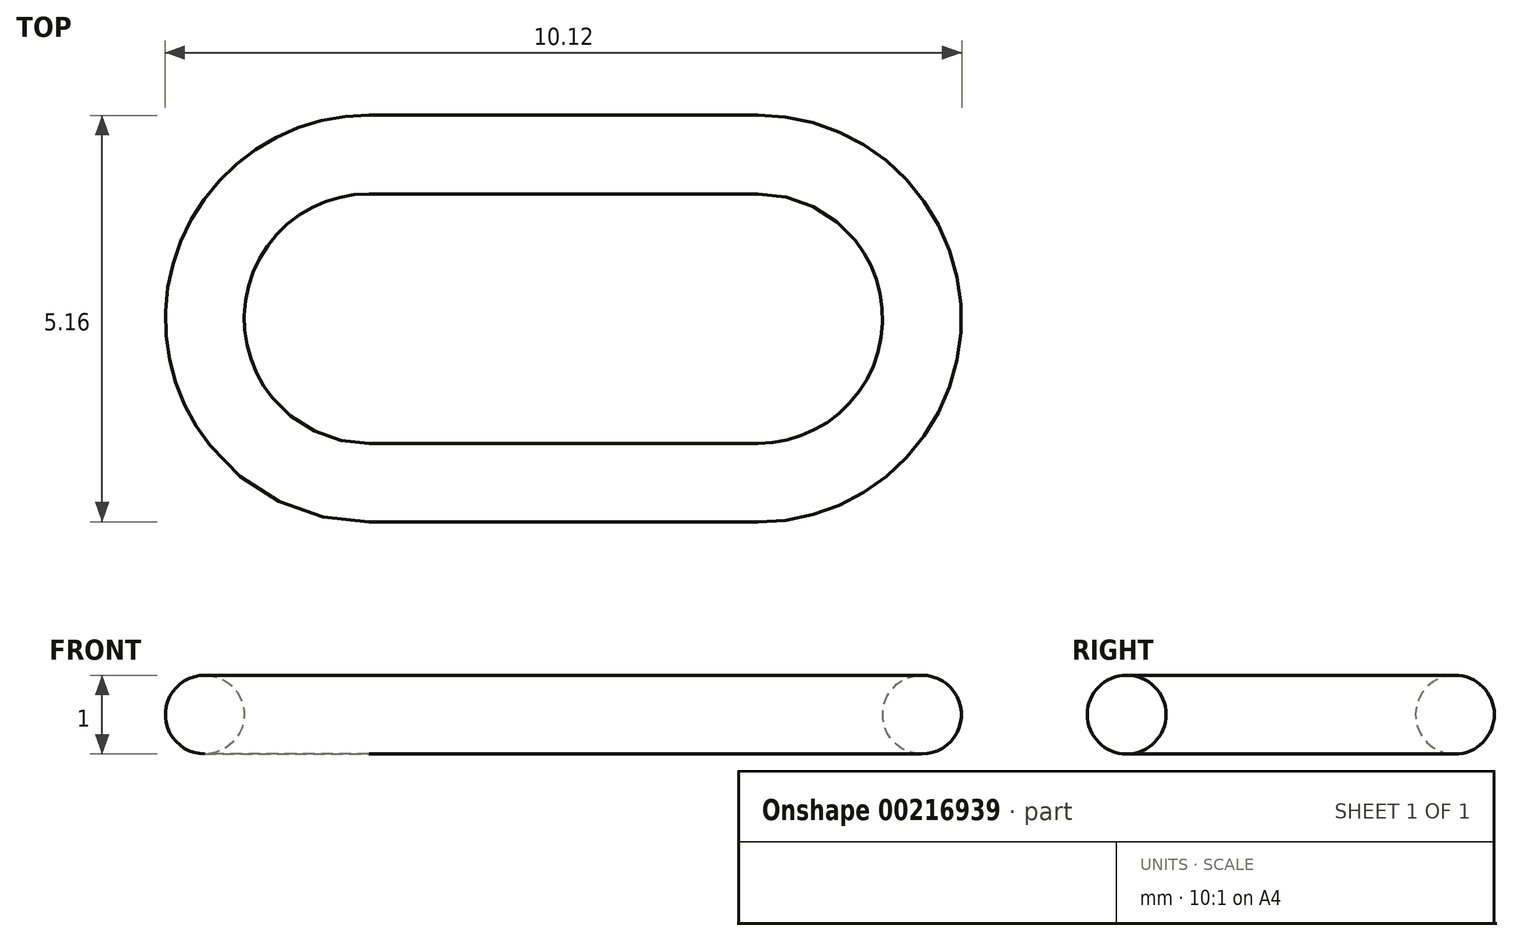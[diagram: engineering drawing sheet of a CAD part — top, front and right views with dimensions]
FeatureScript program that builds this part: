
annotation { "Feature Type Name" : "Feature", "Feature Type Description" : "" }
export const myFeature = defineFeature(function(context is Context, id is Id, definition is map)
    precondition{}
    {
        {
            var Q0;
            Q0=qCreatedBy(makeId("Top.planeOp"),FACE);
            var sketch = newSketch(context, id + "F0", { "sketchPlane" : qUnion([Q0])});
            skLineSegment(sketch, "E0", {"start": v(-2.47, 1.58) * mm, "end": v(2.47, 1.58) * mm, "construction": true});
            skArc(sketch, "E1", {"start": v(2.47, -1.58) * mm, "mid": v(4.06, 0) * mm, "end": v(2.47, 1.58) * mm, "construction": true});
            skLineSegment(sketch, "E2", {"start": v(2.47, -1.58) * mm, "end": v(-2.47, -1.58) * mm, "construction": true});
            skArc(sketch, "E3", {"start": v(-2.47, 1.58) * mm, "mid": v(-4.06, 0) * mm, "end": v(-2.47, -1.58) * mm, "construction": true});
            skLineSegment(sketch, "E4", {"start": v(0, 1.58) * mm, "end": v(0, -1.58) * mm, "construction": true});
            skLineSegment(sketch, "E5", {"start": v(-4.06, 0) * mm, "end": v(4.06, 0) * mm, "construction": true});
            skLineSegment(sketch, "E6.0", {"start": v(2.47, -2.08) * mm, "end": v(-2.47, -2.08) * mm});
            skArc(sketch, "E6.1", {"start": v(2.47, -2.08) * mm, "mid": v(4.56, 0) * mm, "end": v(2.47, 2.08) * mm});
            skLineSegment(sketch, "E6.2", {"start": v(-2.47, 2.08) * mm, "end": v(2.47, 2.08) * mm});
            skArc(sketch, "E6.3", {"start": v(-2.47, 2.08) * mm, "mid": v(-4.56, 0) * mm, "end": v(-2.47, -2.08) * mm});
            skSolve(sketch);
        }
        {
            var Q0;
            Q0=qCreatedBy(makeId("Right.planeOp"),FACE);
            var Q1;
            Q1=sQuery(id+"F0.wireOp",VERTEX,"E6.2.start");
            cPlane(context, id + "F1", {"entities" : qUnion([Q0, Q1]), "cplaneType" : CPlaneType.PLANE_POINT, "offset" : 25 * mm, "width" : 150 * mm, "height" : 150 * mm});
        }
        {
            var Q0;
            Q0=qCreatedBy(id+"F1.planeOp",FACE);
            var sketch = newSketch(context, id + "F2", { "sketchPlane" : qUnion([Q0])});
            skCircle(sketch, "E7", {"center": v(2.08, 0) * mm, "radius": 0.5 * mm});
            skSolve(sketch);
        }
        {
            var Q0;
            Q0 = qSketchRegion(id + "F2", true);
            var Q1;
            Q1 = qConstructionFilter(qBodyType(qCreatedBy(id + "F0" ,EDGE), BodyType.WIRE), ConstructionObject.NO);
            sweep(context, id + "F3", {"profiles" : qUnion([Q0]), "path" : qUnion([Q1])});
        }
    });
